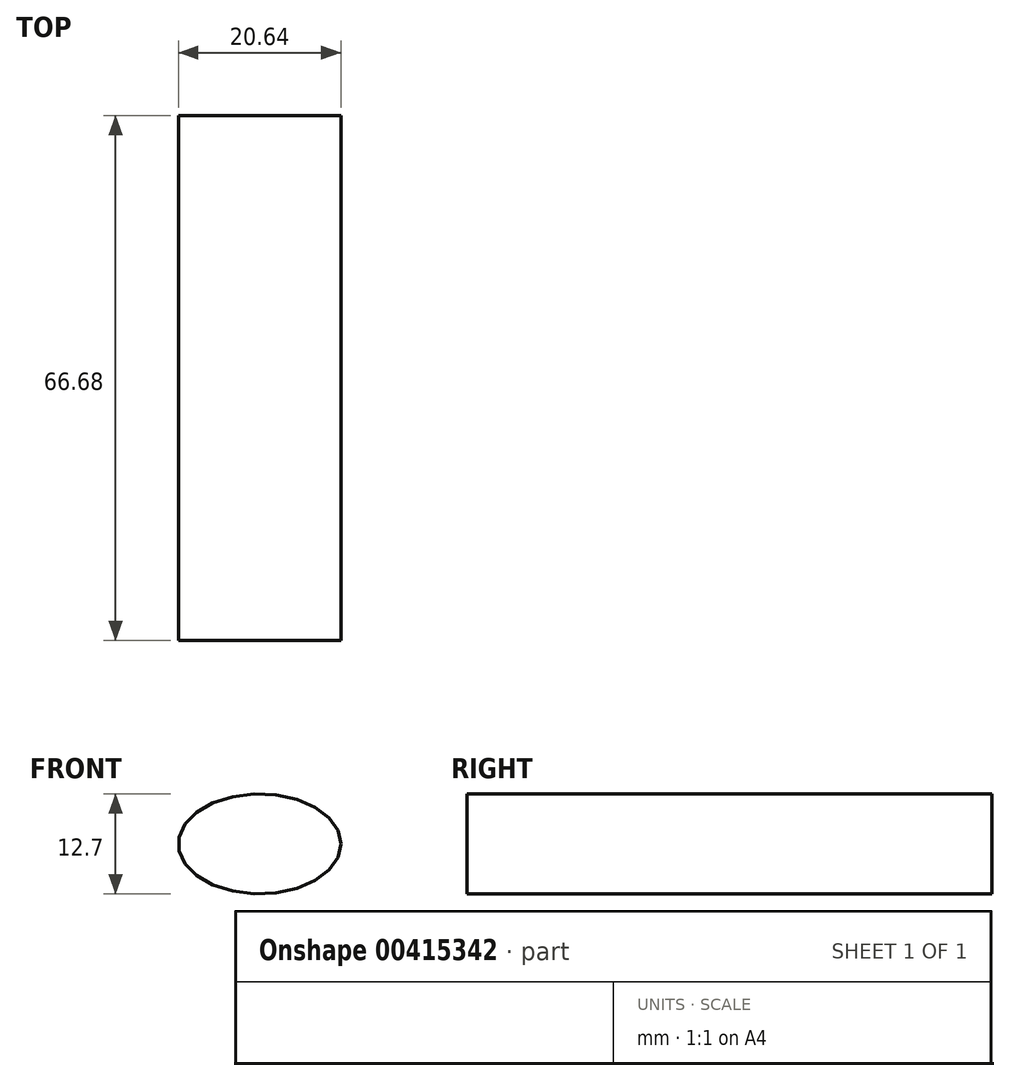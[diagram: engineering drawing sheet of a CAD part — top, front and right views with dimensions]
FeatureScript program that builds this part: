
annotation { "Feature Type Name" : "Feature", "Feature Type Description" : "" }
export const myFeature = defineFeature(function(context is Context, id is Id, definition is map)
    precondition{}
    {
        {
            var Q0;
            Q0=qCreatedBy(makeId("Front.planeOp"),FACE);
            var sketch = newSketch(context, id + "F0", { "sketchPlane" : qUnion([Q0])});
            skEllipse(sketch, "E0", {"center": v(0, 0) * mm, "majorRadius": 10.32 * mm, "minorRadius": 6.35 * mm, "majorAxis": v(1, 0)});
            skSolve(sketch);
        }
        {
            var Q0;
            Q0 = qSketchRegion(id + "F0", true);
            extrude(context, id + "F1", {"entities" : qUnion([Q0]), "oppositeDirection" : true, "depth" : 66.67 * mm});
        }
    });
